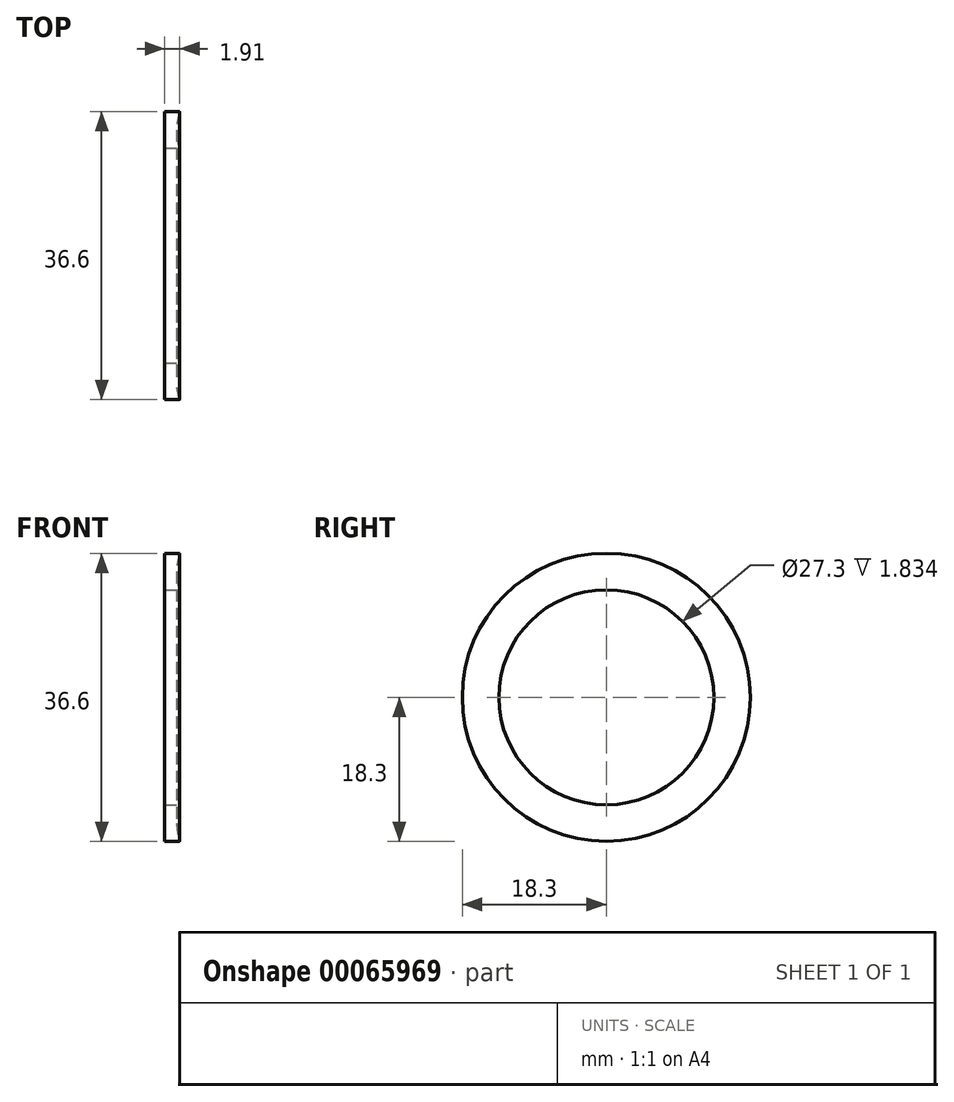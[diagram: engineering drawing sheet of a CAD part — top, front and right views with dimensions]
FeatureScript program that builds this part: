
annotation { "Feature Type Name" : "Feature", "Feature Type Description" : "" }
export const myFeature = defineFeature(function(context is Context, id is Id, definition is map)
    precondition{}
    {
        {
            var Q0;
            Q0=qCreatedBy(makeId("Front.planeOp"),FACE);
            var sketch = newSketch(context, id + "F0", { "sketchPlane" : qUnion([Q0])});
            skLineSegment(sketch, "E0.bottom", {"start": v(-0.1, 18.3) * mm, "end": v(-1.94, 18.3) * mm});
            skLineSegment(sketch, "E0.top", {"start": v(-0.1, 13.65) * mm, "end": v(-1.94, 13.65) * mm});
            skLineSegment(sketch, "E0.right", {"start": v(-1.94, 18.3) * mm, "end": v(-1.94, 13.65) * mm});
            skLineSegment(sketch, "E1", {"start": v(0, 0) * mm, "end": v(-6.16, 0) * mm, "construction": true});
            skArc(sketch, "E2", {"start": v(-0.04, 18.2) * mm, "mid": v(-0.42, 15.98) * mm, "end": v(-0.04, 13.75) * mm});
            skPoint(sketch, "E3.visualSharp", {"position": v(0, 18.3) * mm});
            skArc(sketch, "E3.filletArc", {"start": v(-0.04, 18.2) * mm, "mid": v(-0.05, 18.27) * mm, "end": v(-0.1, 18.3) * mm});
            skPoint(sketch, "E4.visualSharp", {"position": v(0, 13.65) * mm});
            skArc(sketch, "E4.filletArc", {"start": v(-0.1, 13.65) * mm, "mid": v(-0.05, 13.68) * mm, "end": v(-0.04, 13.75) * mm});
            skLineSegment(sketch, "E5", {"start": v(0, 13.65) * mm, "end": v(0, 0) * mm, "construction": true});
            skSolve(sketch);
        }
        {
            var Q0;
            Q0=makeQuery(id+"F0.imprint","IMPRINT",FACE,{"disambiguationData":[TD([[makeQuery(id+"F0.imprint","IMPRINT",EDGE,{"derivedFrom":sQuery(id+"F0.wireOp",EDGE,"E0.bottom")}),1.0]])]});
            var Q1;
            Q1=sQuery(id+"F0.wireOp",EDGE,"E1");
            revolve(context, id + "F1", {"entities" : qUnion([Q0]), "axis" : qUnion([Q1]), "revolveType" : RevolveType.FULL});
        }
    });
